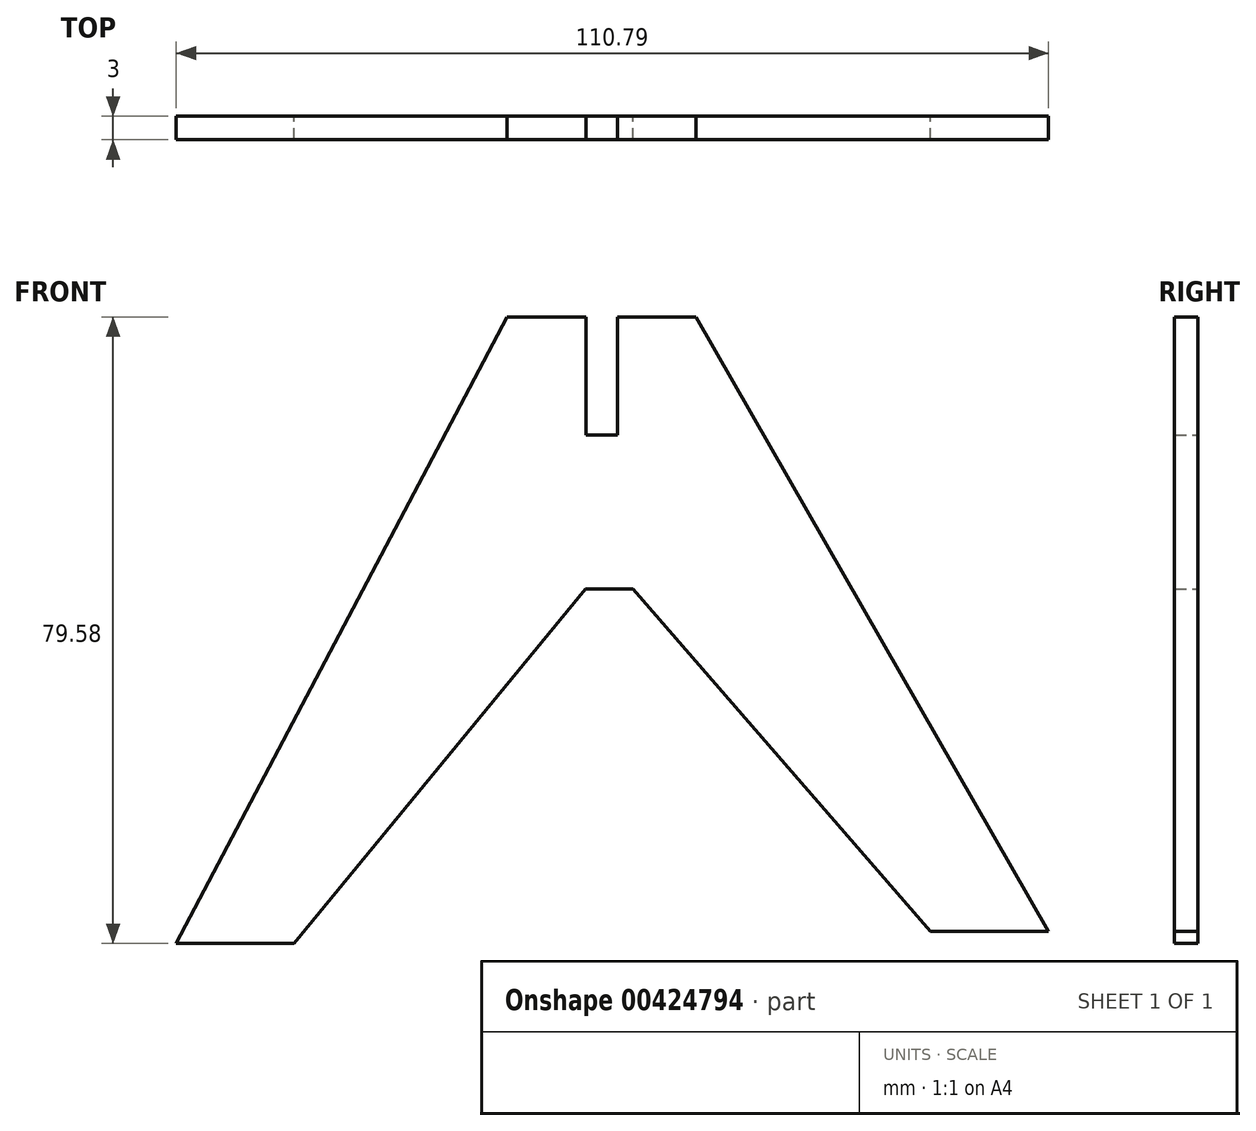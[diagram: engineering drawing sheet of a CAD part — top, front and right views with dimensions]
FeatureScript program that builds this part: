
annotation { "Feature Type Name" : "Feature", "Feature Type Description" : "" }
export const myFeature = defineFeature(function(context is Context, id is Id, definition is map)
    precondition{}
    {
        {
            var Q0;
            Q0=qCreatedBy(makeId("Front.planeOp"),FACE);
            var sketch = newSketch(context, id + "F0", { "sketchPlane" : qUnion([Q0])});
            skLineSegment(sketch, "E0", {"start": v(-95.8, -64.58) * mm, "end": v(-80.8, -64.58) * mm});
            skLineSegment(sketch, "E1", {"start": v(0, -63.08) * mm, "end": v(15, -63.08) * mm});
            skPoint(sketch, "E2.start.orphan", {"position": v(119.24, 0) * mm});
            skLineSegment(sketch, "E3", {"start": v(-41.76, 0) * mm, "end": v(-39.76, 0) * mm});
            skLineSegment(sketch, "E4", {"start": v(-41.76, 0) * mm, "end": v(-43.76, 0) * mm});
            skLineSegment(sketch, "E5", {"start": v(-39.76, 0) * mm, "end": v(-39.76, 15) * mm});
            skLineSegment(sketch, "E6", {"start": v(-43.76, 0) * mm, "end": v(-43.76, 15) * mm});
            skLineSegment(sketch, "E7", {"start": v(-39.76, 15) * mm, "end": v(-29.76, 15) * mm});
            skLineSegment(sketch, "E8", {"start": v(-43.76, 15) * mm, "end": v(-53.76, 15) * mm});
            skLineSegment(sketch, "E9", {"start": v(-53.76, 15) * mm, "end": v(-95.8, -64.58) * mm});
            skLineSegment(sketch, "E10", {"start": v(-29.76, 15) * mm, "end": v(15, -63.08) * mm});
            skLineSegment(sketch, "E11", {"start": v(-40.8, -19.58) * mm, "end": v(-37.8, -19.58) * mm});
            skLineSegment(sketch, "E12", {"start": v(-40.8, -19.58) * mm, "end": v(-43.8, -19.58) * mm});
            skLineSegment(sketch, "E13", {"start": v(-43.8, -19.58) * mm, "end": v(-80.8, -64.58) * mm});
            skLineSegment(sketch, "E14", {"start": v(-37.8, -19.58) * mm, "end": v(0, -63.08) * mm});
            skPoint(sketch, "E15.orphan", {"position": v(-40.4, -63.83) * mm});
            skSolve(sketch);
        }
        {
            var Q0;
            Q0=makeQuery(id+"F0.imprint","IMPRINT",FACE,{"disambiguationData":[TD([[makeQuery(id+"F0.imprint","IMPRINT",EDGE,{"derivedFrom":sQuery(id+"F0.wireOp",EDGE,"E0")}),1.0]])]});
            extrude(context, id + "F1", {"entities" : qUnion([Q0]), "depth" : 3 * mm});
        }
    });
